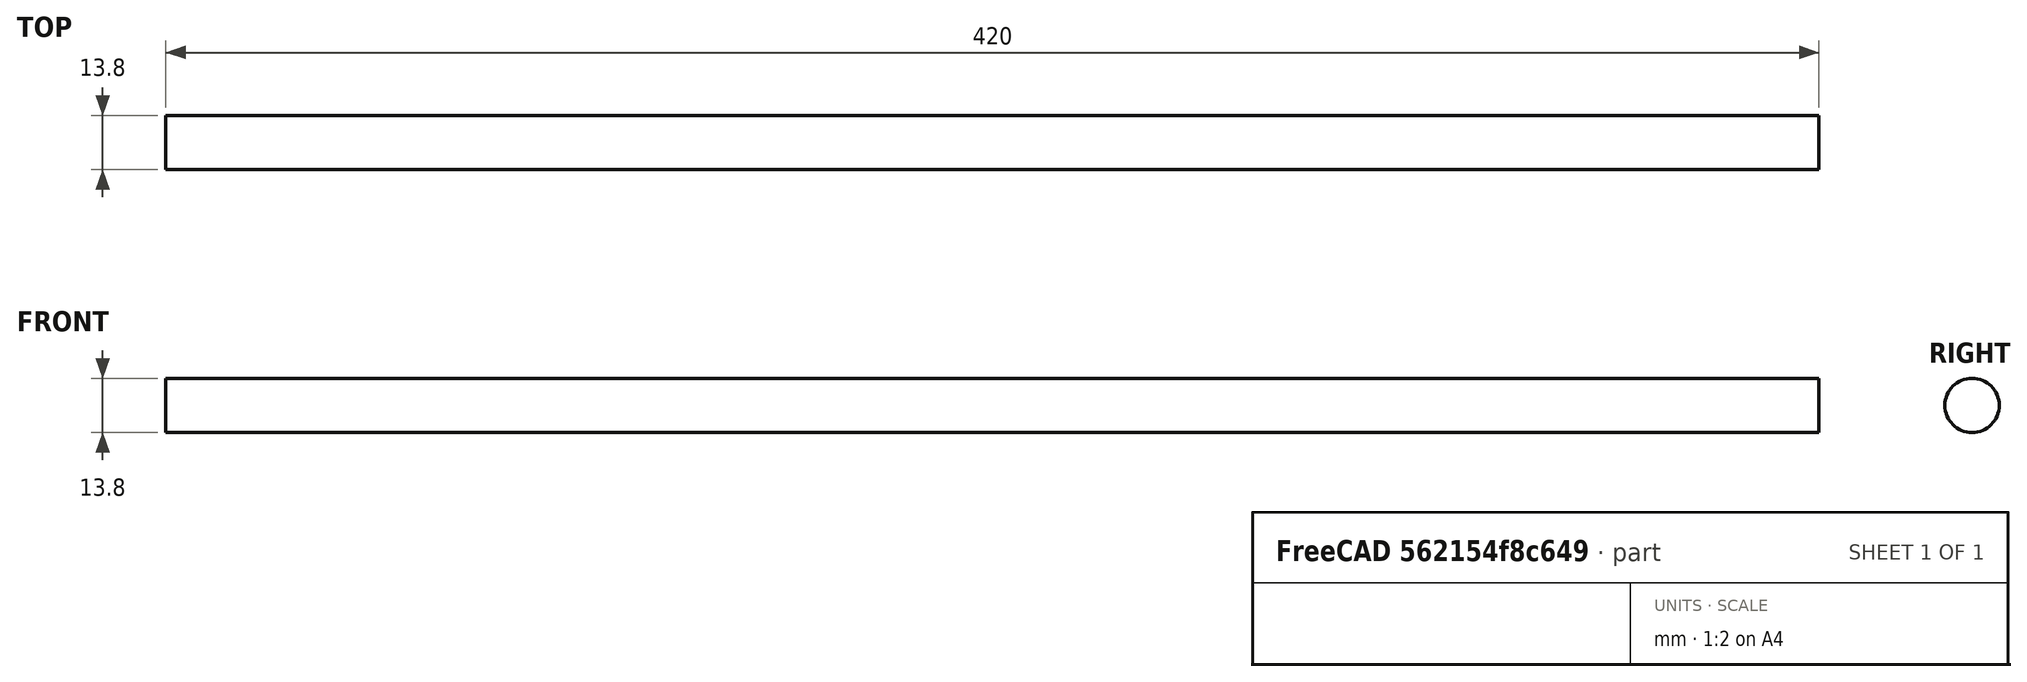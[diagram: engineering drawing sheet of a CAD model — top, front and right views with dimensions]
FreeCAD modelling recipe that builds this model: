
FCSTD DOCUMENT  (FreeCAD 0.19R)
Label: PlotterRail
License: All rights reserved
LicenseURL: http://en.wikipedia.org/wiki/All_rights_reserved
objects: App::DocumentObjectGroup×3, PartDesign::CoordinateSystem×2, App::FeaturePython×1, Sketcher::SketchObject×1, PartDesign::Pad×1, PartDesign::Body×1, App::Part×1
note: 6 computed .brp shape members not serialized (recipe doc carries the construction recipe); baked Part::Feature solids carry a one-line shape summary decoded from their .brp

FEATURE [App::DocumentObjectGroup] Parts
FEATURE [PartDesign::CoordinateSystem] LCS_Origin
  AttacherType = Attacher::AttachEngine3D
  MapMode = 2
  Support = -> [X_Axis]
FEATURE [App::DocumentObjectGroup] Constraints
FEATURE [App::FeaturePython] Variables  # WARN: FeaturePython — macro-defined, semantics opaque (R4)
  Type = App::PropertyContainer
FEATURE [App::DocumentObjectGroup] Configurations
FEATURE [Sketcher::SketchObject] Sketch
  FullyConstrained = true
  Placement = pos=(0,0,0) rot=(0.57735,0.57735,0.57735;2.0944rad)
  sketch-geometry (1):
    g0: Circle CenterX=0 CenterY=0 CenterZ=0 NormalX=0 NormalY=0 NormalZ=1 AngleXU=0 Radius=6.9
  constraints (2):
    c: Coincident(g0,g-1)
    c: Radius(g0) = 6.9  'X-Axis'
FEATURE [PartDesign::Pad] Pad
  Direction = (1,1,1)
  Length = 420
  Length2 = 100
  Midplane = true
  Placement = pos=(0,0,0) rot=(0.57735,0.57735,0.57735;2.0944rad)
  Profile = -> Sketch
  Refine = true
  Type = 0
FEATURE [PartDesign::Body] Body  label="X_Axis_Rail1"
  Group = -> [Sketch,Pad]
  Origin = -> Origin001
  Tip = -> Pad
FEATURE [PartDesign::CoordinateSystem] LCS_1
  AttacherType = Attacher::AttachEngine3D
  AttachmentOffset = pos=(0,0,0) rot=(0,1,0;1.5708rad)
  MapMode = 11
  Placement = pos=(210,-9e-16,2.4e-14) rot=(0,0,1;3.14159rad)
  Support = -> [Pad]
FEATURE [App::Part] Model
  AssemblyType = Part::Link
  Group = -> [LCS_Origin,Constraints,Variables,Configurations,LCS_1,Body]
  Origin = -> Origin
  Type = Assembly
